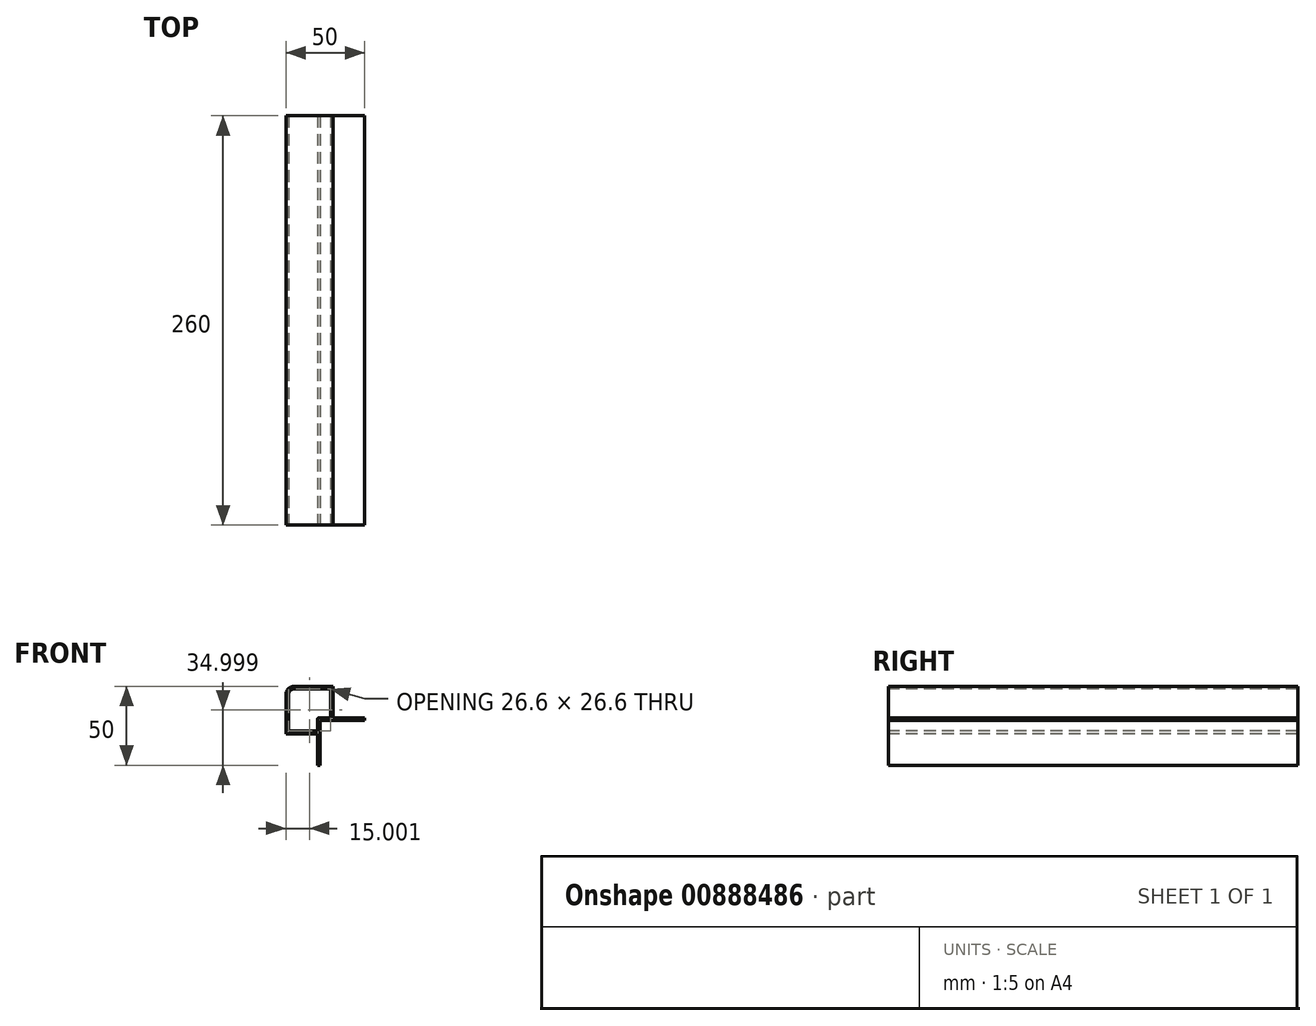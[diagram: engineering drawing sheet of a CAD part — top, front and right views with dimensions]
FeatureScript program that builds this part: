
annotation { "Feature Type Name" : "Feature", "Feature Type Description" : "" }
export const myFeature = defineFeature(function(context is Context, id is Id, definition is map)
    precondition{}
    {
        {
            var Q0;
            Q0=qCreatedBy(makeId("Front.planeOp"),FACE);
            var sketch = newSketch(context, id + "F0", { "sketchPlane" : qUnion([Q0])});
            skLineSegment(sketch, "E0.bottom", {"start": v(-14.05, 19.05) * mm, "end": v(10.95, 19.05) * mm});
            skLineSegment(sketch, "E0.top", {"start": v(-19.05, -10.95) * mm, "end": v(0.95, -10.95) * mm});
            skLineSegment(sketch, "E0.left", {"start": v(-19.05, 14.05) * mm, "end": v(-19.05, -10.95) * mm});
            skLineSegment(sketch, "E0.right", {"start": v(10.95, 19.05) * mm, "end": v(10.95, -0.95) * mm});
            skPoint(sketch, "E0.middle", {"position": v(-4.05, 4.05) * mm});
            skLineSegment(sketch, "E1", {"start": v(0.95, -1.95) * mm, "end": v(0.95, -9.25) * mm});
            skLineSegment(sketch, "E2", {"start": v(1.95, -0.95) * mm, "end": v(9.25, -0.95) * mm});
            skPoint(sketch, "E3.orphan", {"position": v(10.95, -10.95) * mm});
            skLineSegment(sketch, "E4", {"start": v(30.95, -0.95) * mm, "end": v(30.95, -2.65) * mm});
            skLineSegment(sketch, "E5", {"start": v(30.95, -2.65) * mm, "end": v(2.65, -2.65) * mm});
            skLineSegment(sketch, "E6", {"start": v(2.65, -2.65) * mm, "end": v(2.65, -30.95) * mm});
            skLineSegment(sketch, "E7", {"start": v(2.65, -30.95) * mm, "end": v(0.95, -30.95) * mm});
            skLineSegment(sketch, "E8.trimOffspring", {"start": v(10.95, -0.95) * mm, "end": v(30.95, -0.95) * mm});
            skLineSegment(sketch, "E9.trimOffspring", {"start": v(0.95, -10.95) * mm, "end": v(0.95, -30.95) * mm});
            skPoint(sketch, "E10.visualSharp", {"position": v(-19.05, 19.05) * mm});
            skArc(sketch, "E10.filletArc", {"start": v(-14.05, 19.05) * mm, "mid": v(-17.58, 17.58) * mm, "end": v(-19.05, 14.05) * mm});
            skLineSegment(sketch, "E11.0", {"start": v(-14.05, 17.35) * mm, "end": v(9.25, 17.35) * mm});
            skLineSegment(sketch, "E12.0", {"start": v(-17.35, 14.05) * mm, "end": v(-17.35, -9.25) * mm});
            skArc(sketch, "E12.1", {"start": v(-14.05, 17.35) * mm, "mid": v(-16.38, 16.38) * mm, "end": v(-17.35, 14.05) * mm});
            skLineSegment(sketch, "E13.0", {"start": v(9.25, 17.35) * mm, "end": v(9.25, -0.95) * mm});
            skLineSegment(sketch, "E14.0", {"start": v(-17.35, -9.25) * mm, "end": v(0.95, -9.25) * mm});
            skPoint(sketch, "E15.visualSharp", {"position": v(0.95, -0.95) * mm});
            skArc(sketch, "E15.filletArc", {"start": v(1.95, -0.95) * mm, "mid": v(1.24, -1.24) * mm, "end": v(0.95, -1.95) * mm});
            skSolve(sketch);
        }
        {
            var Q0;
            Q0=makeQuery(id+"F0.imprint","IMPRINT",FACE,{"disambiguationData":[TD([[makeQuery(id+"F0.imprint","IMPRINT",EDGE,{"derivedFrom":sQuery(id+"F0.wireOp",EDGE,"E0.bottom")}),-1.0]])]});
            extrude(context, id + "F1", {"entities" : qUnion([Q0]), "oppositeDirection" : true, "depth" : 260 * mm, "offsetDistance" : 25 * mm});
        }
    });
